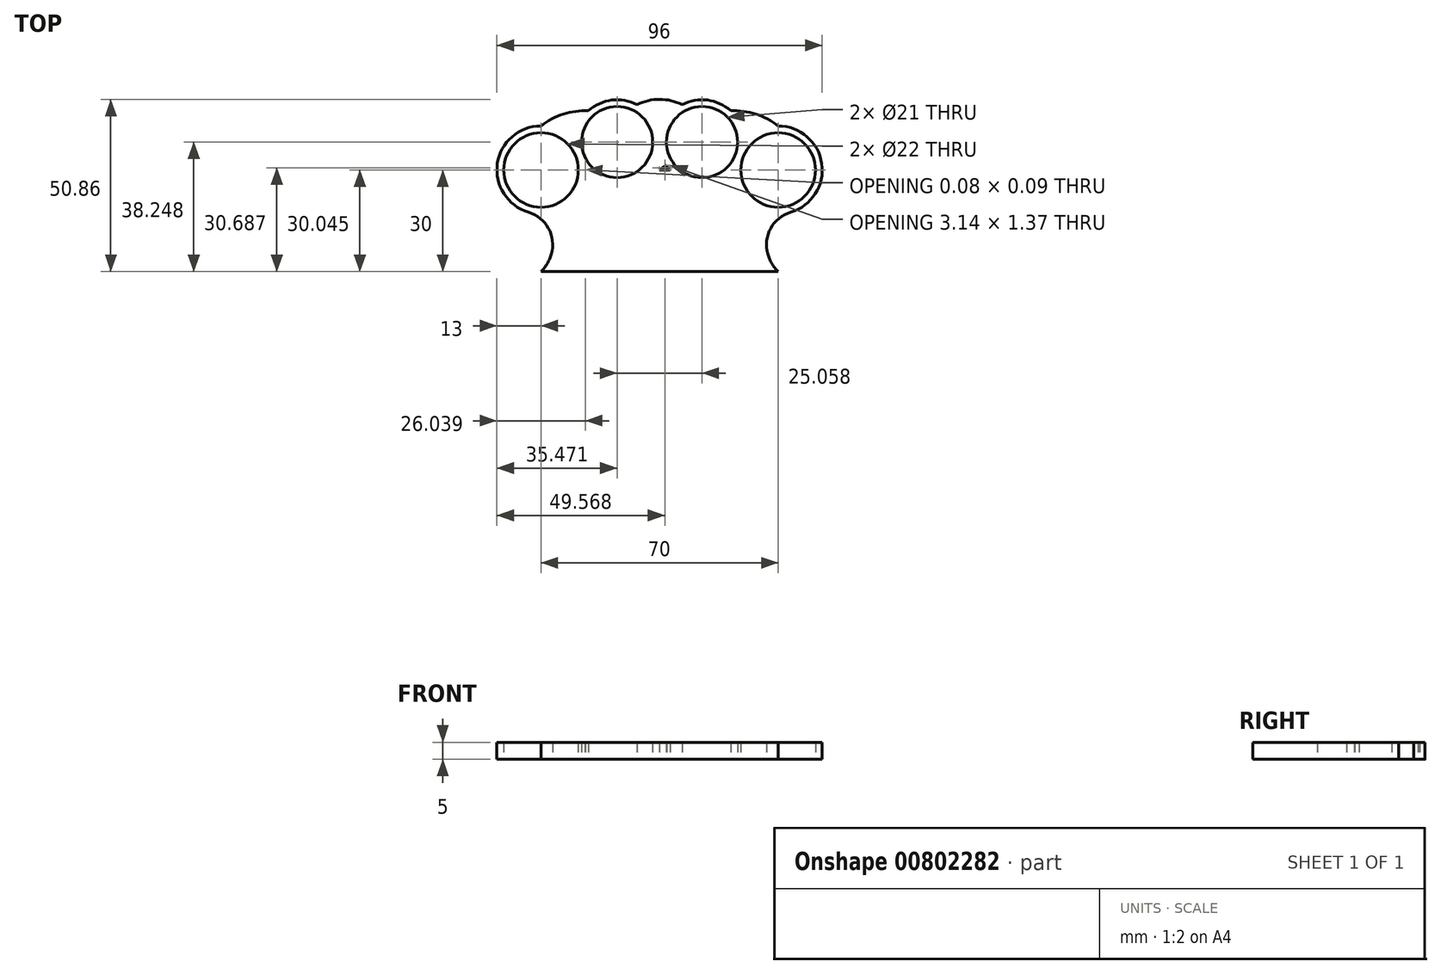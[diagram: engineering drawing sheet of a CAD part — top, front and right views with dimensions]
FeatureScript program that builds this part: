
annotation { "Feature Type Name" : "Feature", "Feature Type Description" : "" }
export const myFeature = defineFeature(function(context is Context, id is Id, definition is map)
    precondition{}
    {
        {
            var Q0;
            Q0=qCreatedBy(makeId("Top.planeOp"),FACE);
            var sketch = newSketch(context, id + "F0", { "sketchPlane" : qUnion([Q0])});
            skLineSegment(sketch, "E0", {"start": v(0, 0) * mm, "end": v(-35, 0) * mm});
            skLineSegment(sketch, "E1", {"start": v(0, 0) * mm, "end": v(35, 0) * mm});
            skArc(sketch, "E2", {"start": v(35, 0) * mm, "mid": v(0, 9.38) * mm, "end": v(-35, 0) * mm});
            skCircle(sketch, "E3", {"center": v(-35, 0) * mm, "radius": 11 * mm});
            skLineSegment(sketch, "E4", {"start": v(0, 0) * mm, "end": v(0, 9.38) * mm});
            skCircle(sketch, "E5", {"center": v(-12.53, 8.25) * mm, "radius": 10.5 * mm});
            skCircle(sketch, "E6.MirrorC", {"center": v(12.53, 8.25) * mm, "radius": 10.5 * mm});
            skCircle(sketch, "E7", {"center": v(35, 0) * mm, "radius": 11 * mm});
            skLineSegment(sketch, "E8", {"start": v(12.53, 8.25) * mm, "end": v(0, 0) * mm});
            skLineSegment(sketch, "E9", {"start": v(-35, 0) * mm, "end": v(-50, 0) * mm});
            skCircle(sketch, "E10.0", {"center": v(-35, 0) * mm, "radius": 13 * mm});
            skCircle(sketch, "E11.0", {"center": v(-12.53, 8.25) * mm, "radius": 12.5 * mm});
            skCircle(sketch, "E12.0", {"center": v(12.53, 8.25) * mm, "radius": 12.5 * mm});
            skCircle(sketch, "E13.0", {"center": v(35, 0) * mm, "radius": 13 * mm});
            skLineSegment(sketch, "E14", {"start": v(35, 0) * mm, "end": v(50, 0) * mm});
            skArc(sketch, "E15", {"start": v(-20.97, 17.46) * mm, "mid": v(-28.4, 16.5) * mm, "end": v(-35, 13) * mm});
            skArc(sketch, "E16", {"start": v(4.09, 17.46) * mm, "mid": v(0, 18.03) * mm, "end": v(-4.09, 17.46) * mm});
            skArc(sketch, "E17", {"start": v(35, 13) * mm, "mid": v(28.4, 16.5) * mm, "end": v(20.97, 17.46) * mm});
            skLineSegment(sketch, "E18", {"start": v(0, 0) * mm, "end": v(0, -30) * mm});
            skLineSegment(sketch, "E19", {"start": v(0, -30) * mm, "end": v(-35, -30) * mm});
            skLineSegment(sketch, "E20", {"start": v(0, -30) * mm, "end": v(35, -30) * mm});
            skArc(sketch, "E21", {"start": v(-35, -30) * mm, "mid": v(-31.47, -21.5) * mm, "end": v(-35, -13) * mm});
            skArc(sketch, "E22", {"start": v(6.67, 19.29) * mm, "mid": v(0, 20.86) * mm, "end": v(-6.68, 19.3) * mm});
            skArc(sketch, "E23", {"start": v(35, -13) * mm, "mid": v(31.47, -21.5) * mm, "end": v(35, -30) * mm});
            skSolve(sketch);
        }
        {
            var Q0;
            {var subQ7=sQuery(id+"F0.wireOp",EDGE,"E18");Q0=makeQuery(id+"F0.imprint","IMPRINT",FACE,{"disambiguationData":[TD([[makeQuery(id+"F0.imprint","IMPRINT",EDGE,{"derivedFrom":subQ7}),-1.0]])]});}
            var Q1;
            {var subQ7=sQuery(id+"F0.wireOp",EDGE,"E18");Q1=makeQuery(id+"F0.imprint","IMPRINT",FACE,{"disambiguationData":[TD([[makeQuery(id+"F0.imprint","IMPRINT",EDGE,{"derivedFrom":subQ7}),1.0]])]});}
            var Q2;
            {var subQ0=sQuery(id+"F0.wireOp",EDGE,"E12.0");var subQ1=sQuery(id+"F0.wireOp",EDGE,"E1");var subQ2=makeQuery(id+"F0.imprint","INTERSECT",VERTEX,{"disambiguationData":[OD(0.0)],"derivedFrom":[subQ1,subQ0]});Q2=makeQuery(id+"F0.imprint","IMPRINT",FACE,{"disambiguationData":[TD([[makeQuery(id+"F0.imprint","IMPRINT",EDGE,{"disambiguationData":[TD([[subQ2,-1.0]])],"derivedFrom":subQ1}),-1.0]])]});}
            var Q3;
            {var subQ0=sQuery(id+"F0.wireOp",EDGE,"E13.0");var subQ4=sQuery(id+"F0.wireOp",EDGE,"E1");var subQ5=makeQuery(id+"F0.imprint","INTERSECT",VERTEX,{"derivedFrom":[subQ4,subQ0]});Q3=makeQuery(id+"F0.imprint","IMPRINT",FACE,{"disambiguationData":[TD([[makeQuery(id+"F0.imprint","IMPRINT",EDGE,{"disambiguationData":[TD([[subQ5,-1.0]])],"derivedFrom":subQ4}),-1.0]])]});}
            var Q4;
            {var subQ3=sQuery(id+"F0.wireOp",EDGE,"E13.0");var subQ6=sQuery(id+"F0.wireOp",EDGE,"E1");var subQ9=makeQuery(id+"F0.imprint","INTERSECT",VERTEX,{"derivedFrom":[subQ6,subQ3]});Q4=makeQuery(id+"F0.imprint","IMPRINT",FACE,{"disambiguationData":[TD([[makeQuery(id+"F0.imprint","IMPRINT",EDGE,{"disambiguationData":[TD([[subQ9,-1.0]])],"derivedFrom":subQ6}),1.0]])]});}
            var Q5;
            {var subQ5=sQuery(id+"F0.wireOp",EDGE,"E2");var subQ8=sQuery(id+"F0.wireOp",EDGE,"E7");var subQ9=makeQuery(id+"F0.imprint","INTERSECT",VERTEX,{"derivedFrom":[subQ5,subQ8]});Q5=makeQuery(id+"F0.imprint","IMPRINT",FACE,{"disambiguationData":[TD([[makeQuery(id+"F0.imprint","IMPRINT",EDGE,{"disambiguationData":[TD([[subQ9,-1.0]])],"derivedFrom":subQ5}),-1.0]])]});}
            var Q6;
            {var subQ2=sQuery(id+"F0.wireOp",EDGE,"E2");var subQ4=sQuery(id+"F0.wireOp",EDGE,"E13.0");var subQ5=makeQuery(id+"F0.imprint","INTERSECT",VERTEX,{"derivedFrom":[subQ2,subQ4]});Q6=makeQuery(id+"F0.imprint","IMPRINT",FACE,{"disambiguationData":[TD([[makeQuery(id+"F0.imprint","IMPRINT",EDGE,{"disambiguationData":[TD([[subQ5,-1.0]])],"derivedFrom":subQ2}),-1.0]])]});}
            var Q7;
            {var subQ0=sQuery(id+"F0.wireOp",EDGE,"E6.MirrorC");var subQ1=sQuery(id+"F0.wireOp",EDGE,"E2");var subQ2=makeQuery(id+"F0.imprint","INTERSECT",VERTEX,{"disambiguationData":[OD(1.0)],"derivedFrom":[subQ1,subQ0]});Q7=makeQuery(id+"F0.imprint","IMPRINT",FACE,{"disambiguationData":[TD([[makeQuery(id+"F0.imprint","IMPRINT",EDGE,{"disambiguationData":[TD([[subQ2,-1.0]])],"derivedFrom":subQ1}),1.0]])]});}
            var Q8;
            {var subQ0=sQuery(id+"F0.wireOp",EDGE,"E12.0");var subQ1=sQuery(id+"F0.wireOp",EDGE,"E1");var subQ2=makeQuery(id+"F0.imprint","INTERSECT",VERTEX,{"disambiguationData":[OD(0.0)],"derivedFrom":[subQ1,subQ0]});Q8=makeQuery(id+"F0.imprint","IMPRINT",FACE,{"disambiguationData":[TD([[makeQuery(id+"F0.imprint","IMPRINT",EDGE,{"disambiguationData":[TD([[subQ2,-1.0]])],"derivedFrom":subQ1}),1.0]])]});}
            var Q9;
            {var subQ0=sQuery(id+"F0.wireOp",EDGE,"E6.MirrorC");var subQ1=sQuery(id+"F0.wireOp",EDGE,"E1");var subQ2=makeQuery(id+"F0.imprint","INTERSECT",VERTEX,{"disambiguationData":[OD(1.0)],"derivedFrom":[subQ1,subQ0]});Q9=makeQuery(id+"F0.imprint","IMPRINT",FACE,{"disambiguationData":[TD([[makeQuery(id+"F0.imprint","IMPRINT",EDGE,{"disambiguationData":[TD([[subQ2,-1.0]])],"derivedFrom":subQ1}),1.0]])]});}
            var Q10;
            {var subQ0=sQuery(id+"F0.wireOp",EDGE,"E12.0");var subQ1=sQuery(id+"F0.wireOp",EDGE,"E2");var subQ2=makeQuery(id+"F0.imprint","INTERSECT",VERTEX,{"disambiguationData":[OD(0.0)],"derivedFrom":[subQ1,subQ0]});Q10=makeQuery(id+"F0.imprint","IMPRINT",FACE,{"disambiguationData":[TD([[makeQuery(id+"F0.imprint","IMPRINT",EDGE,{"disambiguationData":[TD([[subQ2,-1.0]])],"derivedFrom":subQ1}),1.0]])]});}
            var Q11;
            {var subQ0=sQuery(id+"F0.wireOp",EDGE,"E12.0");var subQ1=sQuery(id+"F0.wireOp",EDGE,"E2");var subQ2=makeQuery(id+"F0.imprint","INTERSECT",VERTEX,{"disambiguationData":[OD(0.0)],"derivedFrom":[subQ1,subQ0]});Q11=makeQuery(id+"F0.imprint","IMPRINT",FACE,{"disambiguationData":[TD([[makeQuery(id+"F0.imprint","IMPRINT",EDGE,{"disambiguationData":[TD([[subQ2,-1.0]])],"derivedFrom":subQ1}),-1.0]])]});}
            var Q12;
            {var subQ0=sQuery(id+"F0.wireOp",EDGE,"E12.0");var subQ1=sQuery(id+"F0.wireOp",EDGE,"E1");var subQ2=makeQuery(id+"F0.imprint","INTERSECT",VERTEX,{"disambiguationData":[OD(1.0)],"derivedFrom":[subQ1,subQ0]});Q12=makeQuery(id+"F0.imprint","IMPRINT",FACE,{"disambiguationData":[TD([[makeQuery(id+"F0.imprint","IMPRINT",EDGE,{"disambiguationData":[TD([[subQ2,-1.0]])],"derivedFrom":subQ1}),1.0]])]});}
            var Q13;
            {var subQ0=sQuery(id+"F0.wireOp",EDGE,"E4");Q13=makeQuery(id+"F0.imprint","IMPRINT",FACE,{"disambiguationData":[TD([[makeQuery(id+"F0.imprint","IMPRINT",EDGE,{"derivedFrom":subQ0}),1.0]])]});}
            var Q14;
            {var subQ0=sQuery(id+"F0.wireOp",EDGE,"E4");Q14=makeQuery(id+"F0.imprint","IMPRINT",FACE,{"disambiguationData":[TD([[makeQuery(id+"F0.imprint","IMPRINT",EDGE,{"derivedFrom":subQ0}),-1.0]])]});}
            var Q15;
            {var subQ1=sQuery(id+"F0.wireOp",EDGE,"E1");var subQ3=sQuery(id+"F0.wireOp",EDGE,"E12.0");var subQ4=makeQuery(id+"F0.imprint","INTERSECT",VERTEX,{"disambiguationData":[OD(0.0)],"derivedFrom":[subQ1,subQ3]});Q15=makeQuery(id+"F0.imprint","IMPRINT",FACE,{"disambiguationData":[TD([[makeQuery(id+"F0.imprint","IMPRINT",EDGE,{"disambiguationData":[TD([[subQ4,-1.0]])],"derivedFrom":subQ3}),1.0]])]});}
            var Q16;
            {var subQ0=sQuery(id+"F0.wireOp",EDGE,"E11.0");var subQ1=sQuery(id+"F0.wireOp",EDGE,"E0");var subQ2=makeQuery(id+"F0.imprint","INTERSECT",VERTEX,{"disambiguationData":[OD(0.0)],"derivedFrom":[subQ1,subQ0]});Q16=makeQuery(id+"F0.imprint","IMPRINT",FACE,{"disambiguationData":[TD([[makeQuery(id+"F0.imprint","IMPRINT",EDGE,{"disambiguationData":[TD([[subQ2,-1.0]])],"derivedFrom":subQ1}),-1.0]])]});}
            var Q17;
            {var subQ0=sQuery(id+"F0.wireOp",EDGE,"E11.0");var subQ1=sQuery(id+"F0.wireOp",EDGE,"E0");var subQ2=makeQuery(id+"F0.imprint","INTERSECT",VERTEX,{"disambiguationData":[OD(0.0)],"derivedFrom":[subQ1,subQ0]});Q17=makeQuery(id+"F0.imprint","IMPRINT",FACE,{"disambiguationData":[TD([[makeQuery(id+"F0.imprint","IMPRINT",EDGE,{"disambiguationData":[TD([[subQ2,-1.0]])],"derivedFrom":subQ1}),1.0]])]});}
            var Q18;
            {var subQ1=sQuery(id+"F0.wireOp",EDGE,"E2");var subQ3=sQuery(id+"F0.wireOp",EDGE,"E11.0");var subQ10=makeQuery(id+"F0.imprint","INTERSECT",VERTEX,{"disambiguationData":[OD(0.0)],"derivedFrom":[subQ1,subQ3]});Q18=makeQuery(id+"F0.imprint","IMPRINT",FACE,{"disambiguationData":[TD([[makeQuery(id+"F0.imprint","IMPRINT",EDGE,{"disambiguationData":[TD([[subQ10,-1.0]])],"derivedFrom":subQ1}),-1.0]])]});}
            var Q19;
            {var subQ5=sQuery(id+"F0.wireOp",EDGE,"E0");var subQ7=sQuery(id+"F0.wireOp",EDGE,"E5");var subQ8=makeQuery(id+"F0.imprint","INTERSECT",VERTEX,{"disambiguationData":[OD(1.0)],"derivedFrom":[subQ5,subQ7]});Q19=makeQuery(id+"F0.imprint","IMPRINT",FACE,{"disambiguationData":[TD([[makeQuery(id+"F0.imprint","IMPRINT",EDGE,{"disambiguationData":[TD([[subQ8,-1.0]])],"derivedFrom":subQ5}),-1.0]])]});}
            var Q20;
            {var subQ0=sQuery(id+"F0.wireOp",EDGE,"E10.0");var subQ1=sQuery(id+"F0.wireOp",EDGE,"E2");var subQ2=makeQuery(id+"F0.imprint","INTERSECT",VERTEX,{"derivedFrom":[subQ1,subQ0]});Q20=makeQuery(id+"F0.imprint","IMPRINT",FACE,{"disambiguationData":[TD([[makeQuery(id+"F0.imprint","IMPRINT",EDGE,{"disambiguationData":[TD([[subQ2,-1.0]])],"derivedFrom":subQ1}),1.0]])]});}
            var Q21;
            {var subQ0=sQuery(id+"F0.wireOp",EDGE,"E10.0");var subQ1=sQuery(id+"F0.wireOp",EDGE,"E2");var subQ2=makeQuery(id+"F0.imprint","INTERSECT",VERTEX,{"derivedFrom":[subQ1,subQ0]});Q21=makeQuery(id+"F0.imprint","IMPRINT",FACE,{"disambiguationData":[TD([[makeQuery(id+"F0.imprint","IMPRINT",EDGE,{"disambiguationData":[TD([[subQ2,-1.0]])],"derivedFrom":subQ1}),-1.0]])]});}
            var Q22;
            {var subQ2=sQuery(id+"F0.wireOp",EDGE,"E11.0");var subQ8=sQuery(id+"F0.wireOp",EDGE,"E2");var subQ9=makeQuery(id+"F0.imprint","INTERSECT",VERTEX,{"disambiguationData":[OD(1.0)],"derivedFrom":[subQ8,subQ2]});Q22=makeQuery(id+"F0.imprint","IMPRINT",FACE,{"disambiguationData":[TD([[makeQuery(id+"F0.imprint","IMPRINT",EDGE,{"disambiguationData":[TD([[subQ9,-1.0]])],"derivedFrom":subQ8}),-1.0]])]});}
            var Q23;
            {var subQ0=sQuery(id+"F0.wireOp",EDGE,"E10.0");var subQ5=sQuery(id+"F0.wireOp",EDGE,"E0");var subQ6=makeQuery(id+"F0.imprint","INTERSECT",VERTEX,{"derivedFrom":[subQ5,subQ0]});Q23=makeQuery(id+"F0.imprint","IMPRINT",FACE,{"disambiguationData":[TD([[makeQuery(id+"F0.imprint","IMPRINT",EDGE,{"disambiguationData":[TD([[subQ6,-1.0]])],"derivedFrom":subQ5}),1.0]])]});}
            var Q24;
            {var subQ1=sQuery(id+"F0.wireOp",EDGE,"E0");var subQ7=sQuery(id+"F0.wireOp",EDGE,"E10.0");var subQ8=makeQuery(id+"F0.imprint","INTERSECT",VERTEX,{"derivedFrom":[subQ1,subQ7]});Q24=makeQuery(id+"F0.imprint","IMPRINT",FACE,{"disambiguationData":[TD([[makeQuery(id+"F0.imprint","IMPRINT",EDGE,{"disambiguationData":[TD([[subQ8,-1.0]])],"derivedFrom":subQ1}),-1.0]])]});}
            var Q25;
            {var subQ0=sQuery(id+"F0.wireOp",EDGE,"E16");Q25=makeQuery(id+"F0.imprint","IMPRINT",FACE,{"disambiguationData":[TD([[makeQuery(id+"F0.imprint","IMPRINT",EDGE,{"derivedFrom":subQ0}),1.0]])]});}
            var Q26;
            {var subQ0=sQuery(id+"F0.wireOp",EDGE,"E17");Q26=makeQuery(id+"F0.imprint","IMPRINT",FACE,{"disambiguationData":[TD([[makeQuery(id+"F0.imprint","IMPRINT",EDGE,{"derivedFrom":subQ0}),1.0]])]});}
            var Q27;
            {var subQ0=sQuery(id+"F0.wireOp",EDGE,"E15");Q27=makeQuery(id+"F0.imprint","IMPRINT",FACE,{"disambiguationData":[TD([[makeQuery(id+"F0.imprint","IMPRINT",EDGE,{"derivedFrom":subQ0}),1.0]])]});}
            var Q28;
            {var subQ0=sQuery(id+"F0.wireOp",EDGE,"E16");Q28=makeQuery(id+"F0.imprint","IMPRINT",FACE,{"disambiguationData":[TD([[makeQuery(id+"F0.imprint","IMPRINT",EDGE,{"derivedFrom":subQ0}),-1.0]])]});}
            extrude(context, id + "F1", {"entities" : qUnion([Q0, Q1, Q2, Q3, Q4, Q5, Q6, Q7, Q8, Q9, Q10, Q11, Q12, Q13, Q14, Q15, Q16, Q17, Q18, Q19, Q20, Q21, Q22, Q23, Q24, Q25, Q26, Q27, Q28]), "depth" : 5 * mm, "offsetDistance" : 25 * mm});
        }
        {
            var Q0;
            Q0=makeQuery(id+"F1.opExtrude","SWEPT_EDGE",EDGE,{"disambiguationData":[OSD([sQuery(id+"F0.wireOp",EDGE,"E10.0"),sQuery(id+"F0.wireOp",EDGE,"E21")])]});
            var Q1;
            Q1=makeQuery(id+"F1.opExtrude","SWEPT_EDGE",EDGE,{"disambiguationData":[OSD([sQuery(id+"F0.wireOp",EDGE,"E13.0"),sQuery(id+"F0.wireOp",EDGE,"E23")])]});
            fillet(context, id + "F2", {"entities" : qUnion([Q0, Q1]), "radius" : 10 * mm, "tangentPropagation" : true, "allowEdgeOverflow" : false});
        }
    });
